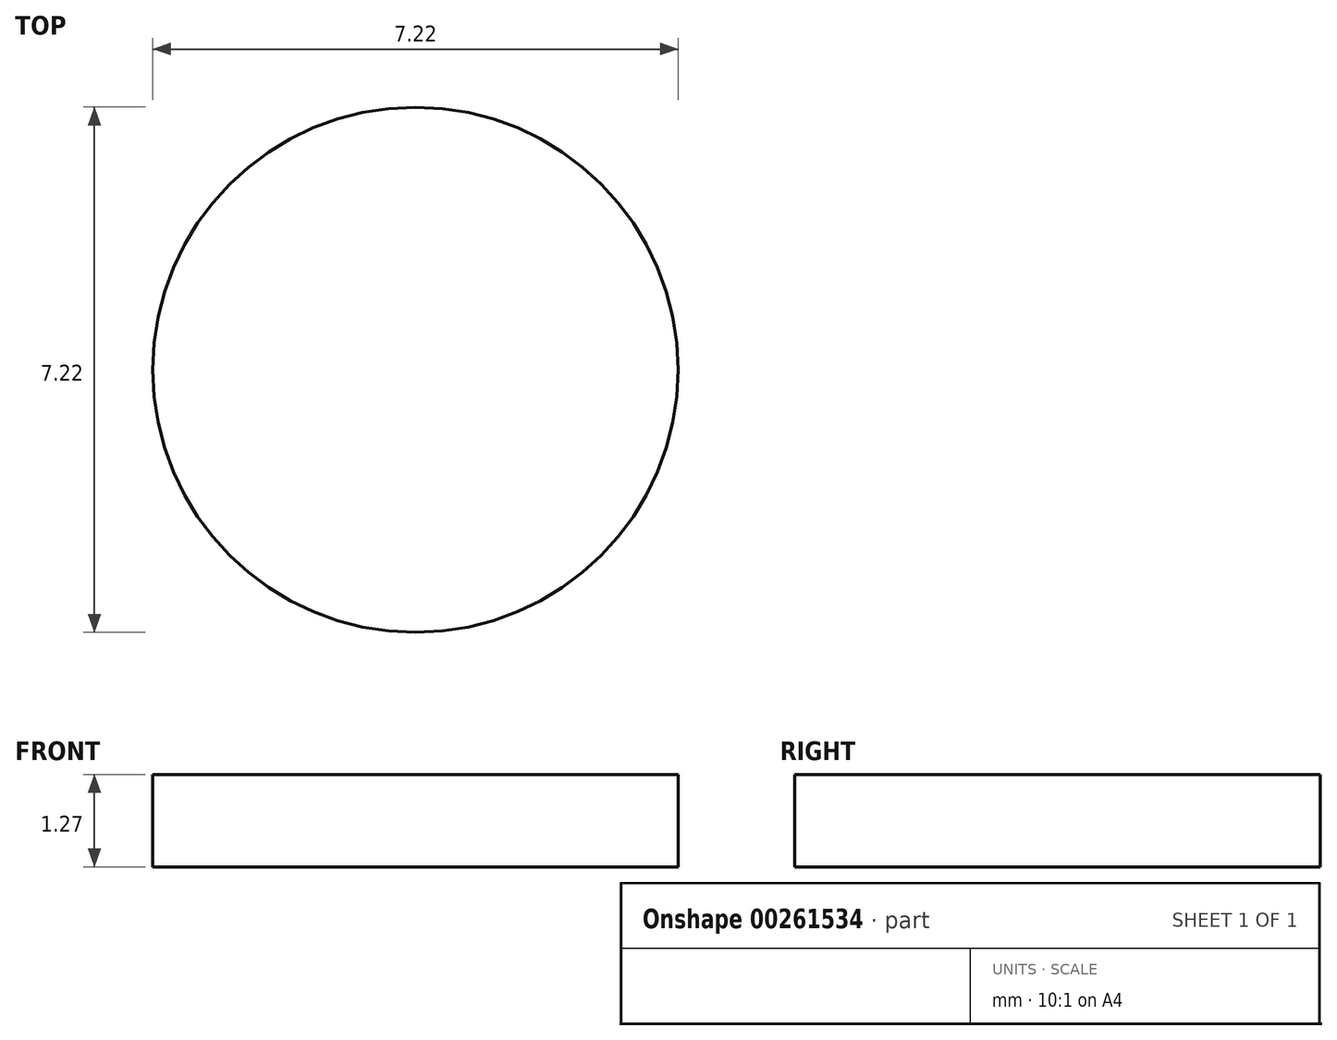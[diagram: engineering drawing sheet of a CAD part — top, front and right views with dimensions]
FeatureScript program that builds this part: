
annotation { "Feature Type Name" : "Feature", "Feature Type Description" : "" }
export const myFeature = defineFeature(function(context is Context, id is Id, definition is map)
    precondition{}
    {
        {
            var Q0;
            Q0=qCreatedBy(makeId("Top.planeOp"),FACE);
            var sketch = newSketch(context, id + "F0", { "sketchPlane" : qUnion([Q0])});
            skCircle(sketch, "E0", {"center": v(0, 0) * mm, "radius": 3.6 * mm});
            skSolve(sketch);
        }
        {
            var Q0;
            Q0=makeQuery(id+"F0.imprint","IMPRINT",FACE,{"disambiguationData":[TD([[makeQuery(id+"F0.imprint","IMPRINT",EDGE,{"derivedFrom":sQuery(id+"F0.wireOp",EDGE,"E0")}),1.0]])]});
            extrude(context, id + "F1", {"entities" : qUnion([Q0]), "depth" : 1.27 * mm});
        }
    });
